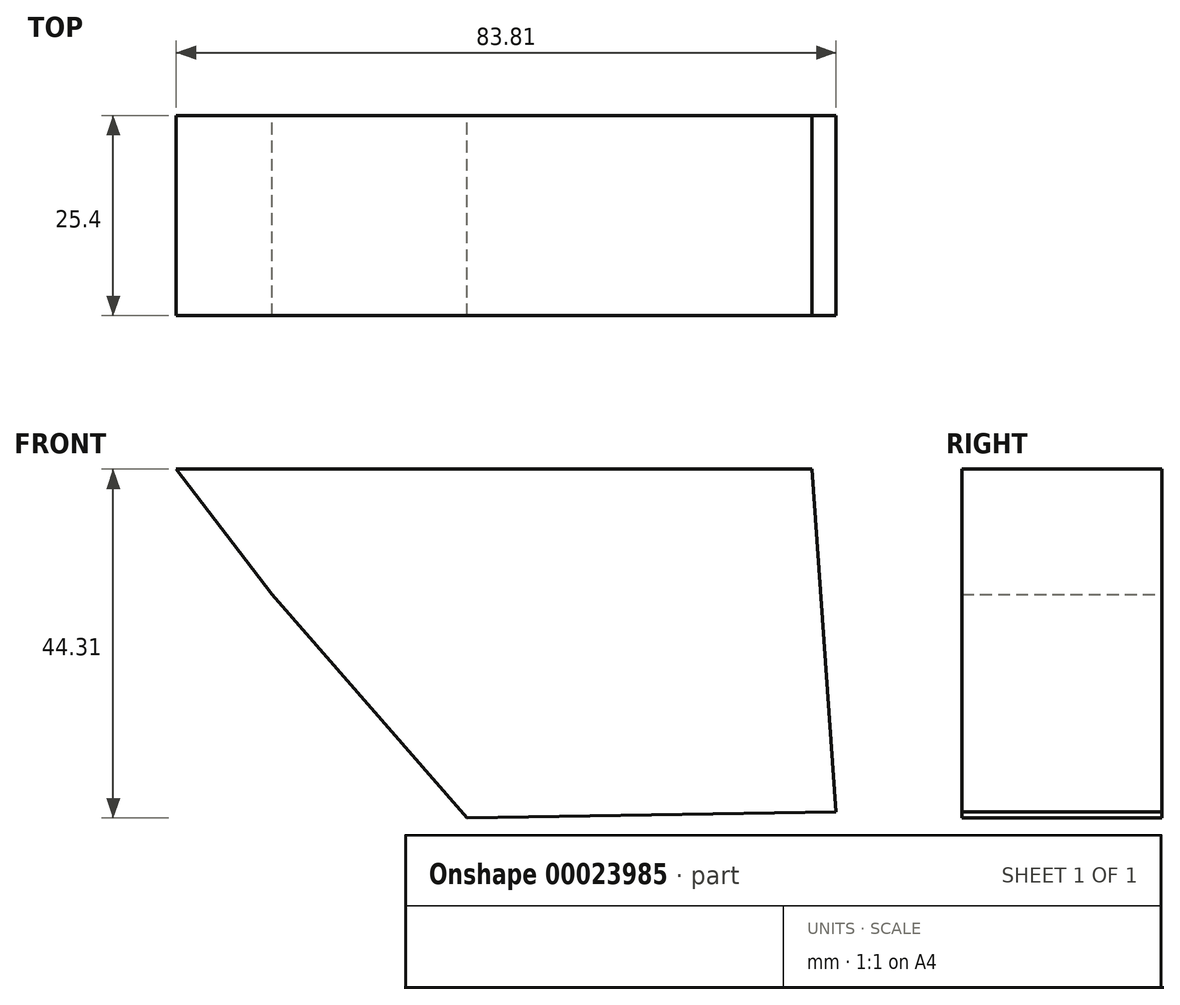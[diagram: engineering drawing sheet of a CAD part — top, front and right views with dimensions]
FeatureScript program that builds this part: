
annotation { "Feature Type Name" : "Feature", "Feature Type Description" : "" }
export const myFeature = defineFeature(function(context is Context, id is Id, definition is map)
    precondition{}
    {
        {
            var Q0;
            Q0=qCreatedBy(makeId("Front.planeOp"),FACE);
            var sketch = newSketch(context, id + "F0", { "sketchPlane" : qUnion([Q0])});
            skLineSegment(sketch, "E0", {"start": v(-47.47, 40) * mm, "end": v(34.3, 40) * mm});
            skLineSegment(sketch, "E1", {"start": v(34.3, 40) * mm, "end": v(37.35, -3.54) * mm});
            skLineSegment(sketch, "E2", {"start": v(37.35, -3.54) * mm, "end": v(-9.5, -4.3) * mm});
            skLineSegment(sketch, "E3", {"start": v(-9.5, -4.3) * mm, "end": v(-34.3, 24.05) * mm});
            skLineSegment(sketch, "E4", {"start": v(-34.3, 24.05) * mm, "end": v(-46.46, 40) * mm});
            skLineSegment(sketch, "E5", {"start": v(-46.46, 40) * mm, "end": v(-46.46, 37.98) * mm});
            skLineSegment(sketch, "E6", {"start": v(-46.46, 37.98) * mm, "end": v(-46.46, 40) * mm});
            skSolve(sketch);
        }
        {
            var Q0;
            {var subQ1=sQuery(id+"F0.wireOp",EDGE,"E1");Q0=makeQuery(id+"F0.imprint","IMPRINT",FACE,{"disambiguationData":[TD([[makeQuery(id+"F0.imprint","IMPRINT",EDGE,{"derivedFrom":subQ1}),-1.0]])]});}
            extrude(context, id + "F1", {"entities" : qUnion([Q0]), "depth" : 25.4 * mm});
        }
    });
